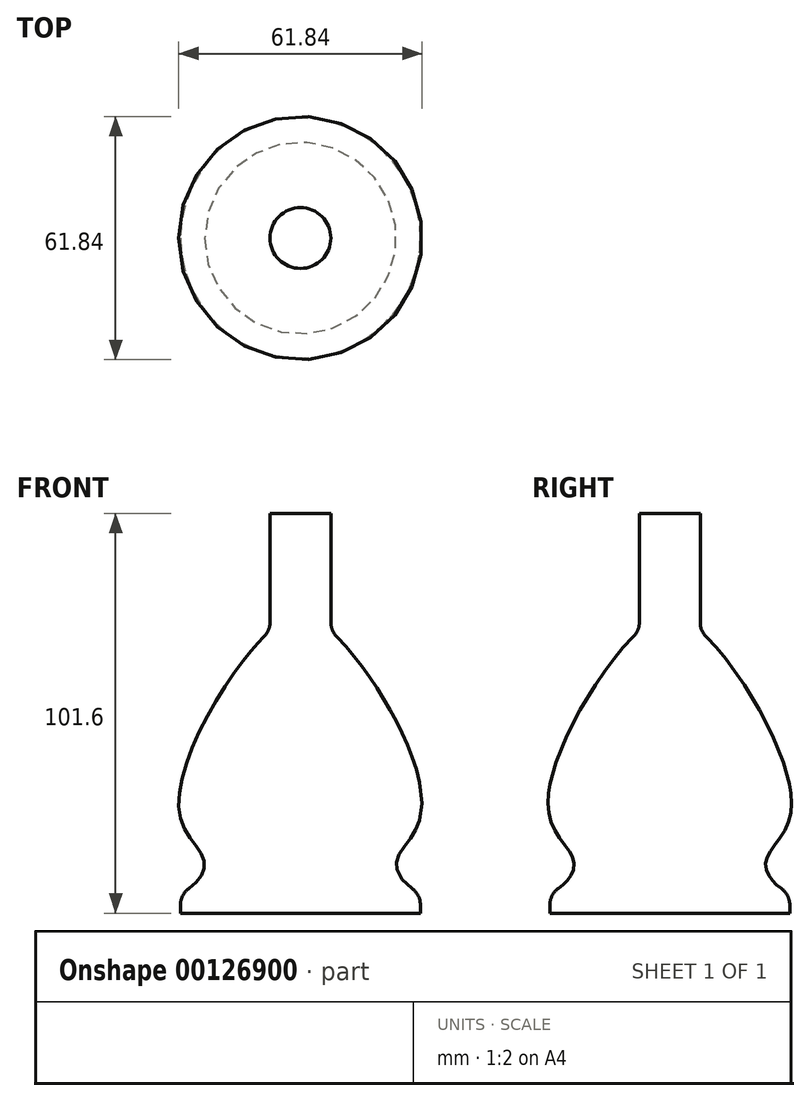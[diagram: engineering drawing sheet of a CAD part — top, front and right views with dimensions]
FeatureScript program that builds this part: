
annotation { "Feature Type Name" : "Feature", "Feature Type Description" : "" }
export const myFeature = defineFeature(function(context is Context, id is Id, definition is map)
    precondition{}
    {
        {
            var Q0;
            Q0=qCreatedBy(makeId("Front.planeOp"),FACE);
            var sketch = newSketch(context, id + "F0", { "sketchPlane" : qUnion([Q0])});
            skLineSegment(sketch, "E0", {"start": v(0, 0) * mm, "end": v(30.48, 0) * mm});
            skLineSegment(sketch, "E1", {"start": v(0, 0) * mm, "end": v(0, 71.12) * mm});
            skLineSegment(sketch, "E2", {"start": v(30.48, 0) * mm, "end": v(30.48, 5.08) * mm});
            skFitSpline(sketch, "E3", {"points": [v(30.48, 5.08) * mm, v(24.33, 12.53) * mm, v(30.48, 24.14) * mm, v(19.32, 57.37) * mm, v(8.13, 71.12) * mm, v(7.73, 71.12) * mm], "startDerivative": vector(-53.21, 21.24) * mm, "endDerivative": vector(-8.66, -4.25) * mm});
            skLineSegment(sketch, "E4", {"start": v(0, 71.12) * mm, "end": v(8.13, 71.12) * mm});
            skSolve(sketch);
        }
        {
            var Q0;
            {var subQ0=sQuery(id+"F0.wireOp",EDGE,"E4");var subQ1=sQuery(id+"F0.wireOp",EDGE,"E3");var subQ2=makeQuery(id+"F0.imprint","INTERSECT",VERTEX,{"disambiguationData":[OD(0.0)],"derivedFrom":[subQ1,subQ0]});Q0=makeQuery(id+"F0.imprint","IMPRINT",FACE,{"disambiguationData":[TD([[makeQuery(id+"F0.imprint","IMPRINT",EDGE,{"disambiguationData":[TD([[subQ2,1.0]])],"derivedFrom":subQ1}),1.0]])]});}
            var Q1;
            Q1=makeQuery(id+"F0.imprint","IMPRINT",FACE,{"disambiguationData":[TD([[makeQuery(id+"F0.imprint","IMPRINT",EDGE,{"derivedFrom":sQuery(id+"F0.wireOp",EDGE,"E0")}),1.0]])]});
            var Q2;
            Q2=sQuery(id+"F0.wireOp",EDGE,"E1");
            revolve(context, id + "F1", {"entities" : qUnion([Q0, Q1]), "axis" : qUnion([Q2]), "revolveType" : RevolveType.FULL});
        }
        {
            var Q0;
            Q0=makeQuery(id+"F1.opRevolve","SWEPT_EDGE",EDGE,{"disambiguationData":[OSD([sQuery(id+"F0.wireOp",EDGE,"E2"),sQuery(id+"F0.wireOp",EDGE,"E3")])]});
            fillet(context, id + "F2", {"entities" : qUnion([Q0]), "radius" : 5.08 * mm, "tangentPropagation" : true, "allowEdgeOverflow" : false});
        }
        {
            var Q0;
            Q0=makeQuery(id+"F1.opRevolve","SWEPT_FACE",FACE,{"disambiguationData":[OSD([sQuery(id+"F0.wireOp",EDGE,"E4")])]});
            extrude(context, id + "F3", {"entities" : qUnion([Q0]), "operationType" : NewBodyOperationType.ADD, "depth" : 30.48 * mm});
        }
        {
            var Q0;
            {var subQ0=sQuery(id+"F0.wireOp",EDGE,"E4");var subQ1=sQuery(id+"F0.wireOp",EDGE,"E3");Q0=makeQuery(id+"F3.boolean.opBoolean","MERGE",EDGE,{"derivedFrom":[makeQuery(id+"F1.opRevolve","SWEPT_EDGE",EDGE,{"disambiguationData":[OSD([subQ1,subQ0])]}),makeQuery(id+"F3.opExtrude","CAP_EDGE",EDGE,{"disambiguationData":[OSD([subQ1,subQ0])],"isStart":true})]});}
            fillet(context, id + "F4", {"entities" : qUnion([Q0]), "radius" : 5.08 * mm, "tangentPropagation" : true, "allowEdgeOverflow" : false});
        }
    });
